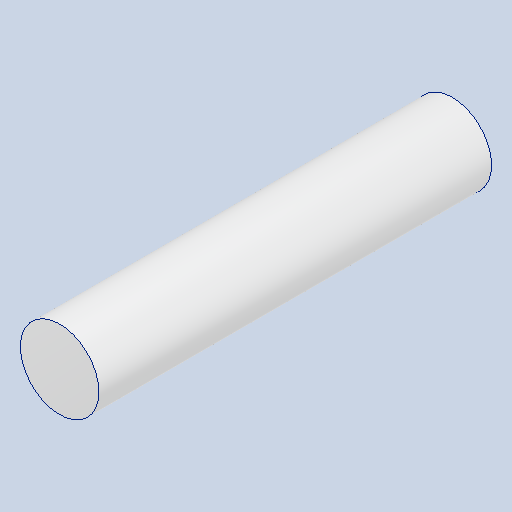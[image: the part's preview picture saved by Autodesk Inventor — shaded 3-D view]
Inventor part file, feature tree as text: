
AUTODESK INVENTOR PART (.ipt)
format: ipt  version: 2024.3 (Build 283343000, 343)  size: 228,864 bytes
history: native  units: mm
features: other x1, extrude x1, sketch x1
ambient origin geometry x8: Origin, YZ Plane, XZ Plane, XY Plane, X Axis, Y Axis, Z Axis, Center Point
bodies: Body1 (feature_tree)
feature tree (3):
  other  "ソリッド1"
  extrude  "押し出し1"  Depth=6.0mm
  sketch  "スケッチ1"
